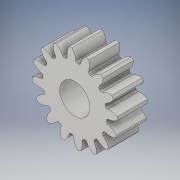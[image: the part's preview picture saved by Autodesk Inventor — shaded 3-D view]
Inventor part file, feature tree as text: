
AUTODESK INVENTOR PART (.ipt)
format: ipt  version: 2019 (Build 230136000, 136)  size: 364,032 bytes
history: native  units: in
note: dims shown in document units (in); Inventor stores cm internally (conversion verified against a paired STEP export)
features: extrude x2, sketch x2, projected_geometry x1, other x1
ambient origin geometry x8: Origin, YZ Plane, XZ Plane, XY Plane, X Axis, Y Axis, Z Axis, Center Point
bodies: Solid1 (feature_tree)
feature tree (6):
  extrude  "Extrusion1"  Depth=0.1979in
  extrude  "Extrusion2"  [1 undecoded]
  sketch  "Sketch1"  dims[d0=0.14in d1=0.0in d2=0.1979in]
  projected_geometry  "Projected Loop1"
  sketch  "Sketch2"  dims[d3=1.0in d4=0.0in]
  other  "bore"
note: 1 required parameter value undecoded (feature->parameter linkage not recoverable at this tier; creation-order binding heuristic only, values carry confidence <= 0.55)
